# Revit family: Deckenhänger TF M10
name_source: partatom
category: HLS-Bauteile
revit_build: Autodesk Revit 2017 (Build: 20190507_1515(x64)
units: mm (PartAtom-declared; Revit-internal decimal feet)

## family parameters
Arbeitsebenenbasiert = Ja
Beim Laden mit Abzugskörper schneiden = Nein
Bemaßung runder Anschluss = Durchmesser verwenden
Gemeinsam genutzt = Ja
Immer vertikal = Nein
Raumberechnungspunkt = Nein
Teiletyp = Normal

## types (1)
- Deckenhänger TF M10
    Artikelnummer = 0816604
    Breite = 70 mm  [stored 0.229659 ft]
    EAN = 4250928420428
    Fabrikat = MEFA
    Firma = MEFA Befestigungs- und Montagesysteme GmbH
    Gewicht = 0.62 kg
    Gewicht pro Bauteil = 0.62 kg
    Gleitreibungsfaktor = 0,15 - 0,25
    Haftreibungsfaktor = 0,2 - 0,3
    Kurztext1 = Deckenhänger TF verst. H 41 mm
    Kurztext2 = für Gewinde M10
    Länge = 146 mm  [stored 0.479003 ft]
    Mengeneinheit = St
    Vorgabe-Ansicht = 1219 mm
    max. Temperaturbeständigkeit = 110 °C
    vpe = 1 St

note: [stored X ft] marks values corroborated as IEEE doubles in the binary element streams (Revit-internal decimal feet)

## geometry (parser evidence)
native form markers: Sweep x3
no freeform markers — native parametric forms only
